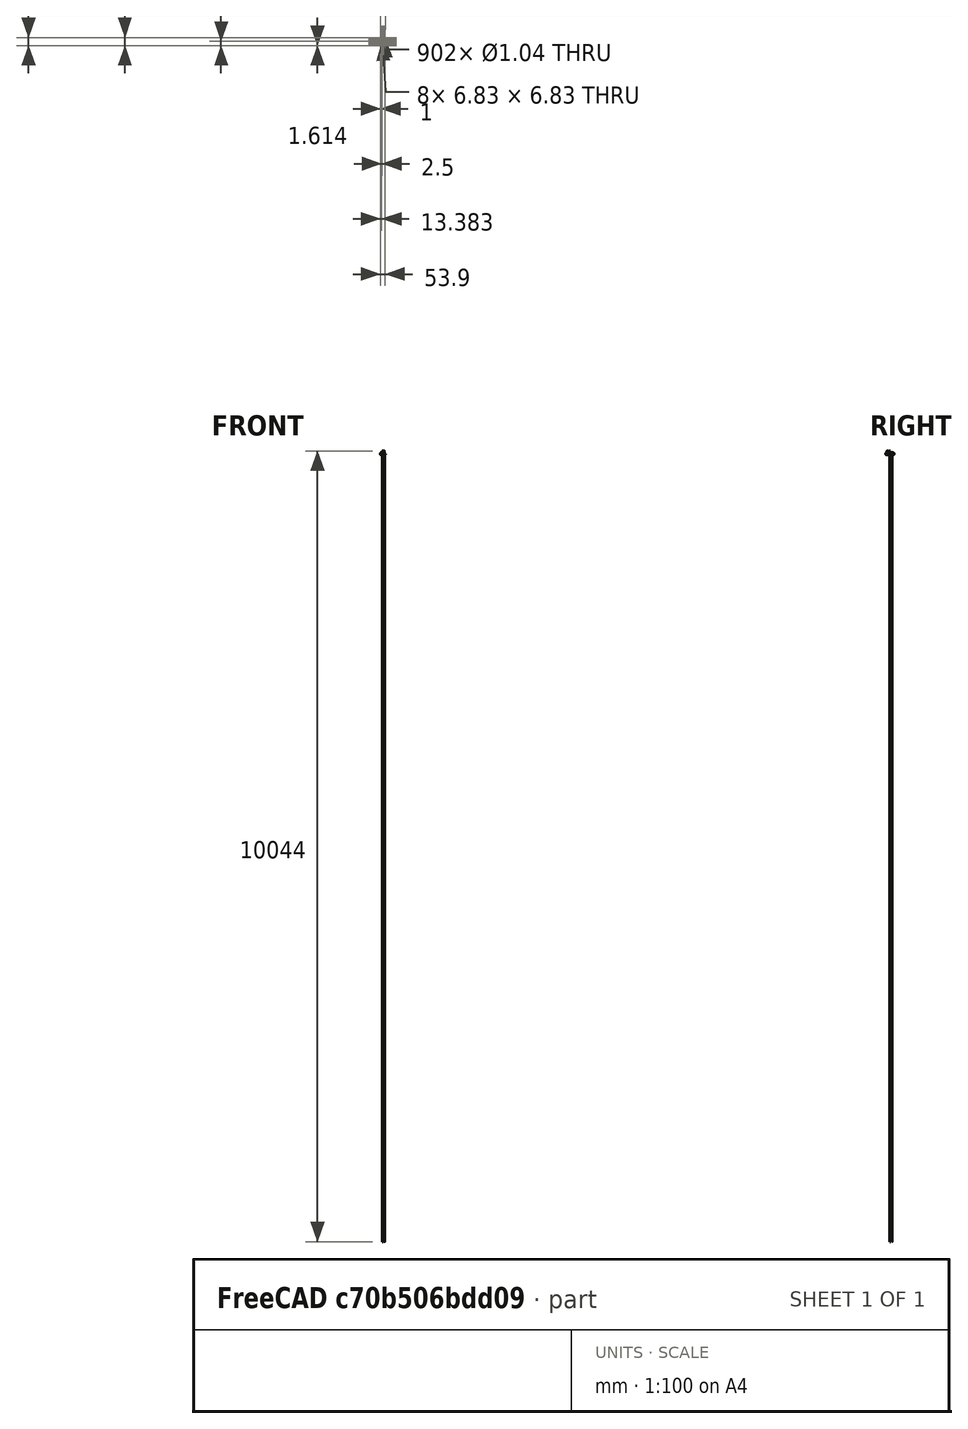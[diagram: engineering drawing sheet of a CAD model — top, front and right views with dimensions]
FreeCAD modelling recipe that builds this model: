
FCSTD DOCUMENT  (FreeCAD 0.16R6603 (Git))
Label: Layouts
License: All rights reserved
LicenseURL: http://en.wikipedia.org/wiki/All_rights_reserved
objects: PartDesign::Pad×12, Sketcher::SketchObject×10, App::DocumentObjectGroup×8, PartDesign::Pocket×5, Part::FeaturePython×4, Part::Feature×2, Part::MultiFuse×2, PartDesign::Fillet×2, PartDesign::LinearPattern×2, PartDesign::Chamfer×1, PartDesign::MultiTransform×1
note: 58 computed .brp shape members not serialized (recipe doc carries the construction recipe); baked Part::Feature solids carry a one-line shape summary decoded from their .brp

FEATURE [Part::Feature] _591A_Box
  Placement = pos=(0,0,1) rot=(1,0,0;3.14159rad)
  shape: bbox 50 x 100 x 21.01 mm, 623 faces (baked)
FEATURE [Part::Feature] _591A_Lid
  Placement = pos=(0,0,1) rot=(0,0,1;1.5708rad)
  shape: bbox 50 x 100 x 5.8 mm, 112 faces (baked)
FEATURE [App::DocumentObjectGroup] Group  label="Box"
  Group = -> [_591A_Lid,_591A_Box]
FEATURE [Sketcher::SketchObject] Sketch
  sketch-geometry (2):
    g0: Circle CenterX=0 CenterY=0 CenterZ=0 NormalX=0 NormalY=0 NormalZ=1 Radius=18.5
    g1: Circle CenterX=0 CenterY=0 CenterZ=0 NormalX=0 NormalY=0 NormalZ=1 Radius=11.5
  constraints (4):
    c: Coincident(g0,g-1)
    c: Radius(g0) = 18.5
    c: Coincident(g1,g-1)
    c: Radius(g1) = 11.5
FEATURE [PartDesign::Pad] Pad
  Length = 0.7
  Length2 = 100
  Sketch = -> Sketch
  Type = 0
FEATURE [Sketcher::SketchObject] Sketch002
  Placement = pos=(0,0,1.5) rot=(0,0,1;0rad)
  sketch-geometry (1):
    g0: Circle CenterX=2.5 CenterY=2.5 CenterZ=0 NormalX=0 NormalY=0 NormalZ=1 Radius=1.9
  constraints (1):
    c: Radius(g0) = 1.9
FEATURE [PartDesign::Pocket] Pocket
  Length = 0.3
  Sketch = -> Sketch002
  Type = 0
FEATURE [Sketcher::SketchObject] Sketch003
  ExternalGeometry = -> [Pocket]
  Placement = pos=(0,0,1.2) rot=(0,0,1;0rad)
  Support = -> Pocket [Face8]
  sketch-geometry (21):
    g0: Circle [constr] CenterX=2.5 CenterY=2.5 CenterZ=0 NormalX=0 NormalY=0 NormalZ=1 Radius=1.66517
    g1: LineSegment StartX=0.835727 StartY=2.55467 StartZ=0 EndX=1.70607 EndY=2.55467 EndZ=0
    g2: LineSegment StartX=1.70607 StartY=2.55467 StartZ=0 EndX=2.17002 EndY=3.01784 EndZ=0
    g3: LineSegment StartX=2.17002 StartY=3.01784 StartZ=0 EndX=2.17002 EndY=3.80753 EndZ=0
    g4: LineSegment StartX=2.17002 StartY=3.80753 StartZ=0 EndX=1.80001 EndY=3.80753 EndZ=0
    g5: LineSegment StartX=1.80001 StartY=3.80753 StartZ=0 EndX=1.80001 EndY=4.01089 EndZ=0
    g6: LineSegment StartX=2.43665 StartY=4.16397 StartZ=0 EndX=2.43665 EndY=2.96848 EndZ=0
    g7: LineSegment StartX=2.43665 StartY=2.96848 StartZ=0 EndX=2.93997 EndY=2.96848 EndZ=0
    g8: LineSegment StartX=2.93997 StartY=2.96848 StartZ=0 EndX=3.51249 EndY=2.38588 EndZ=0
    g9: LineSegment StartX=3.51249 StartY=2.38588 StartZ=0 EndX=4.16126 EndY=2.38588 EndZ=0
    g10: LineSegment StartX=0.847377 StartY=2.29597 StartZ=0 EndX=1.9035 EndY=2.29597 EndZ=0
    g11: LineSegment StartX=1.9035 StartY=2.29597 StartZ=0 EndX=2.26873 EndY=2.70196 EndZ=0
    g12: LineSegment StartX=2.26873 StartY=2.70196 StartZ=0 EndX=2.6537 EndY=2.70196 EndZ=0
    g13: LineSegment StartX=2.6537 StartY=2.70196 StartZ=0 EndX=3.16354 EndY=2.21375 EndZ=0
    g14: LineSegment StartX=3.16354 StartY=2.21375 StartZ=0 EndX=3.16354 EndY=0.972745 EndZ=0
    g15: ArcOfCircle CenterX=2.5 CenterY=2.5 CenterZ=0 NormalX=0 NormalY=0 NormalZ=1 Radius=1.66517 StartAngle=2.00465 EndAngle=3.10875
    g16: ArcOfCircle CenterX=2.5 CenterY=2.5 CenterZ=0 NormalX=0 NormalY=0 NormalZ=1 Radius=1.66517 StartAngle=6.2146 EndAngle=7.89204
    g17: LineSegment StartX=3.41498 StartY=1.10874 StartZ=0 EndX=3.41498 EndY=2.17405 EndZ=0
    g18: LineSegment StartX=3.41498 StartY=2.17405 StartZ=0 EndX=4.13296 EndY=2.17405 EndZ=0
    g19: ArcOfCircle CenterX=2.5 CenterY=2.5 CenterZ=0 NormalX=0 NormalY=0 NormalZ=1 Radius=1.66517 StartAngle=5.29413 EndAngle=6.08617
    g20: ArcOfCircle CenterX=2.5 CenterY=2.5 CenterZ=0 NormalX=0 NormalY=0 NormalZ=1 Radius=1.66517 StartAngle=3.26443 EndAngle=5.12225
  constraints (43):
    c: Coincident(g0,g-3)
    c: PointOnObject(g1,g0)
    c: Horizontal(g1)
    c: Coincident(g1,g2)
    c: Coincident(g2,g3)
    c: Vertical(g3)
    c: Coincident(g3,g4)
    c: Horizontal(g4)
    c: Coincident(g4,g5)
    c: PointOnObject(g5,g0)
    c: PointOnObject(g6,g0)
    c: Vertical(g6)
    c: Coincident(g6,g7)
    c: Horizontal(g7)
    c: Coincident(g7,g8)
    c: Coincident(g8,g9)
    c: PointOnObject(g9,g0)
    c: Horizontal(g9)
    c: PointOnObject(g10,g0)
    c: Horizontal(g10)
    c: Coincident(g10,g11)
    c: Coincident(g11,g12)
    c: Horizontal(g12)
    c: Coincident(g12,g13)
    c: Coincident(g13,g14)
    c: PointOnObject(g14,g0)
    c: Vertical(g14)
    c: Vertical(g5)
    c: Coincident(g15,g1)
    c: Coincident(g15,g5)
    c: Coincident(g16,g6)
    c: Coincident(g16,g9)
    c: PointOnObject(g17,g0)
    c: Vertical(g17)
    c: Coincident(g17,g18)
    c: PointOnObject(g18,g0)
    c: Horizontal(g18)
    c: Coincident(g19,g18)
    c: Coincident(g19,g17)
    c: Tangent(g19,g0)
    c: Coincident(g20,g10)
    c: Coincident(g20,g14)
    c: Tangent(g20,g0)
FEATURE [PartDesign::Pad] Pad002
  Length = 0.1
  Length2 = 100
  Sketch = -> Sketch003
  Type = 0
FEATURE [Part::FeaturePython] Array  # Draft array (typed FeaturePython)
  Angle = 360
  ArrayType = 1
  Axis = (0,0,1)
  Base = -> Pad002
  Center = (-12,0,0)
  Fuse = false
  IntervalAxis = (0,0,0)
  IntervalX = (1,0,0)
  IntervalY = (0,1,0)
  IntervalZ = (0,0,1)
  NumberPolar = 12
  NumberX = 0
  NumberY = 0
  NumberZ = 0
  Placement = pos=(12,0,0) rot=(0,0,1;0rad)
FEATURE [Part::MultiFuse] Fusion
  Placement = pos=(0,-3,22) rot=(0,0,1;0rad)
  Shapes = -> [Array,Pad]
FEATURE [App::DocumentObjectGroup] Group001  label="Neopixel"
  Group = -> [Pocket,Fusion]
FEATURE [PartDesign::Pad] Pad003
  Length = 1
  Length2 = 100
  Placement = pos=(-6,-10,14) rot=(0,0,1;0rad)
  Type = 0
FEATURE [App::DocumentObjectGroup] Group002  label="Knob"
  Group = -> [Pad003]
FEATURE [PartDesign::Pocket] Pocket001
  Length = 1
  Placement = pos=(8,-36,16.3) rot=(0,0,1;0rad)
  Type = 0
FEATURE [PartDesign::Pocket] Pocket002
  Length = 1
  Placement = pos=(-19,-36,36) rot=(0,0,1;0rad)
  Type = 0
FEATURE [PartDesign::Pad] Pad004
  Length = 1
  Length2 = 100
  Placement = pos=(-6,-29,14) rot=(0,0,1;0rad)
  Type = 0
FEATURE [App::DocumentObjectGroup] Group005
FEATURE [Sketcher::SketchObject] Sketch004
  sketch-geometry (4):
    g0: LineSegment StartX=0 StartY=0 StartZ=0 EndX=27 EndY=0 EndZ=0
    g1: LineSegment StartX=27 StartY=0 StartZ=0 EndX=27 EndY=27.3 EndZ=0
    g2: LineSegment StartX=27 StartY=27.3 StartZ=0 EndX=0 EndY=27.3 EndZ=0
    g3: LineSegment StartX=0 StartY=27.3 StartZ=0 EndX=0 EndY=0 EndZ=0
  constraints (11):
    c: Coincident(g0,g1)
    c: Coincident(g1,g2)
    c: Coincident(g2,g3)
    c: Coincident(g3,g0)
    c: Horizontal(g0)
    c: Horizontal(g2)
    c: Vertical(g1)
    c: Vertical(g3)
    c: Coincident(g0,g-1)
    c: DistanceX(g2) = -27
    c: DistanceY(g1) = 27.3
FEATURE [PartDesign::Pad] Pad005
  Length = 1
  Length2 = 100
  Sketch = -> Sketch004
  Type = 0
FEATURE [Sketcher::SketchObject] Sketch001
  ExternalGeometry = -> [Pad005]
  Placement = pos=(0,0,1) rot=(0,0,1;0rad)
  Support = -> Pad005 [Face6]
  sketch-geometry (16):
    g0: ArcOfCircle CenterX=1.75 CenterY=25.175 CenterZ=0 NormalX=0 NormalY=0 NormalZ=1 Radius=1.125 StartAngle=1.5708 EndAngle=4.71239
    g1: ArcOfCircle CenterX=3 CenterY=25.175 CenterZ=0 NormalX=0 NormalY=0 NormalZ=1 Radius=1.125 StartAngle=4.71239 EndAngle=7.85398
    g2: LineSegment StartX=1.75 StartY=24.05 StartZ=0 EndX=3 EndY=24.05 EndZ=0
    g3: LineSegment StartX=1.75 StartY=26.3 StartZ=0 EndX=3 EndY=26.3 EndZ=0
    g4: ArcOfCircle CenterX=24 CenterY=25.175 CenterZ=0 NormalX=0 NormalY=0 NormalZ=1 Radius=1.125 StartAngle=1.5708 EndAngle=4.71239
    g5: ArcOfCircle CenterX=25.25 CenterY=25.175 CenterZ=0 NormalX=0 NormalY=0 NormalZ=1 Radius=1.125 StartAngle=4.71239 EndAngle=7.85398
    g6: LineSegment StartX=24 StartY=24.05 StartZ=0 EndX=25.25 EndY=24.05 EndZ=0
    g7: LineSegment StartX=24 StartY=26.3 StartZ=0 EndX=25.25 EndY=26.3 EndZ=0
    g8: ArcOfCircle CenterX=1.75 CenterY=2.125 CenterZ=0 NormalX=0 NormalY=0 NormalZ=1 Radius=1.125 StartAngle=1.5708 EndAngle=4.71239
    g9: ArcOfCircle CenterX=3 CenterY=2.125 CenterZ=0 NormalX=0 NormalY=0 NormalZ=1 Radius=1.125 StartAngle=4.71239 EndAngle=7.85398
    g10: LineSegment StartX=1.75 StartY=1 StartZ=0 EndX=3 EndY=1 EndZ=0
    g11: LineSegment StartX=1.75 StartY=3.25 StartZ=0 EndX=3 EndY=3.25 EndZ=0
    g12: ArcOfCircle CenterX=24 CenterY=2.125 CenterZ=0 NormalX=0 NormalY=0 NormalZ=1 Radius=1.125 StartAngle=1.5708 EndAngle=4.71239
    g13: ArcOfCircle CenterX=25.25 CenterY=2.125 CenterZ=0 NormalX=0 NormalY=0 NormalZ=1 Radius=1.125 StartAngle=4.71239 EndAngle=7.85398
    g14: LineSegment StartX=24 StartY=1 StartZ=0 EndX=25.25 EndY=1 EndZ=0
    g15: LineSegment StartX=24 StartY=3.25 StartZ=0 EndX=25.25 EndY=3.25 EndZ=0
  constraints (40):
    c: Tangent(g0,g3) = 1.5708
    c: Tangent(g0,g2) = -1.5708
    c: Tangent(g2,g1) = -1.5708
    c: Tangent(g3,g1) = 1.5708
    c: Horizontal(g2)
    c: Equal(g0,g1)
    c: DistanceY(g0,g0) = -2.25
    c: DistanceX(g0,g1) = 1.25
    c: DistanceY(g-3,g0) = -1
    c: DistanceX(g0,g-3) = -1.75
    c: Tangent(g4,g7) = 1.5708
    c: Tangent(g4,g6) = -1.5708
    c: Tangent(g6,g5) = -1.5708
    c: Tangent(g7,g5) = 1.5708
    c: Horizontal(g6)
    c: Equal(g4,g5)
    c: Equal(g6,g2)
    c: Equal(g4,g0)
    c: DistanceX(g-3,g5) = -1.75
    c: DistanceY(g5,g-3) = 1
    c: Tangent(g8,g11) = 1.5708
    c: Tangent(g8,g10) = -1.5708
    c: Tangent(g10,g9) = -1.5708
    c: Tangent(g11,g9) = 1.5708
    c: Horizontal(g10)
    c: Equal(g8,g9)
    c: Equal(g2,g11)
    c: Equal(g9,g0)
    c: DistanceX(g-1,g8) = 1.75
    c: DistanceY(g-1,g8) = 1
    c: Tangent(g12,g15) = 1.5708
    c: Tangent(g12,g14) = -1.5708
    c: Tangent(g14,g13) = -1.5708
    c: Tangent(g15,g13) = 1.5708
    c: Horizontal(g14)
    c: Equal(g12,g13)
    c: Equal(g15,g10)
    c: Equal(g12,g9)
    c: DistanceX(g13,g-4) = 1.75
    c: DistanceY(g13,g-4) = -1
FEATURE [PartDesign::Pocket] Pocket003
  Length = 5
  Sketch = -> Sketch001
  Type = 1
FEATURE [Sketcher::SketchObject] Sketch005
  ExternalGeometry = -> [Pocket003]
  Placement = pos=(0,0,1) rot=(0,0,1;0rad)
  Support = -> Pocket003 [Face5]
  sketch-geometry (4):
    g0: LineSegment StartX=0 StartY=23.1 StartZ=0 EndX=27 EndY=23.1 EndZ=0
    g1: LineSegment StartX=27 StartY=23.1 StartZ=0 EndX=27 EndY=4.1 EndZ=0
    g2: LineSegment StartX=27 StartY=4.1 StartZ=0 EndX=0 EndY=4.1 EndZ=0
    g3: LineSegment StartX=0 StartY=4.1 StartZ=0 EndX=0 EndY=23.1 EndZ=0
  constraints (12):
    c: Coincident(g0,g1)
    c: Coincident(g1,g2)
    c: Coincident(g2,g3)
    c: Coincident(g3,g0)
    c: Horizontal(g0)
    c: Horizontal(g2)
    c: Vertical(g1)
    c: Vertical(g3)
    c: PointOnObject(g0,g-2)
    c: PointOnObject(g1,g-4)
    c: DistanceY(g0,g-4) = 4.2
    c: DistanceY(g3) = 19
FEATURE [PartDesign::Pad] Pad001
  Length = 1.6
  Length2 = 100
  Sketch = -> Sketch005
  Type = 0
FEATURE [Sketcher::SketchObject] Sketch006
  ExternalGeometry = -> [Pad001]
  Placement = pos=(0,0,1) rot=(0,0,1;0rad)
  Support = -> Pad001 [Face7]
  sketch-geometry (4):
    g0: Circle CenterX=9.5 CenterY=25.55 CenterZ=0 NormalX=0 NormalY=0 NormalZ=1 Radius=0.9
    g1: Circle CenterX=11.95 CenterY=25.55 CenterZ=0 NormalX=0 NormalY=0 NormalZ=1 Radius=0.9
    g2: Circle CenterX=14.4 CenterY=25.55 CenterZ=0 NormalX=0 NormalY=0 NormalZ=1 Radius=0.9
    g3: Circle CenterX=16.85 CenterY=25.55 CenterZ=0 NormalX=0 NormalY=0 NormalZ=1 Radius=0.9
  constraints (12):
    c: DistanceX(g-4,g0) = 9.5
    c: DistanceX(g0,g1) = 2.45
    c: DistanceX(g1,g2) = 2.45
    c: DistanceX(g2,g3) = 2.45
    c: Radius(g0) = 0.9
    c: Equal(g0,g1)
    c: Equal(g1,g2)
    c: Equal(g2,g3)
    c: DistanceY(g-4,g0) = -1.75
    c: DistanceY(g1,g-5) = 1.75
    c: DistanceY(g2,g-5) = 1.75
    c: DistanceY(g3,g-5) = 1.75
FEATURE [PartDesign::Pad] Pad006
  Length = 0.5
  Length2 = 100
  Sketch = -> Sketch006
  Type = 0
FEATURE [Part::FeaturePython] Clone  label="Clone of LinearPattern"  # WARN: FeaturePython — macro-defined, semantics opaque (R4)
  Placement = pos=(-13,17,20) rot=(0,0,1;0rad)
  Scale = (1,1,1)
FEATURE [PartDesign::Fillet] Fillet
  Base = -> Pad001 [Edge1]
  Placement = pos=(29.3,0,0) rot=(0.57735,0.57735,0.57735;2.0944rad)
  Radius = 0.3
FEATURE [PartDesign::Fillet] Fillet001
  Base = -> Fillet [Edge3]
  Placement = pos=(29.3,0,0) rot=(0.57735,0.57735,0.57735;2.0944rad)
  Radius = 0.3
FEATURE [PartDesign::Pad] Pad007
  Length = 0.7
  Length2 = 100
  Sketch = -> Sketch003
  Type = 0
FEATURE [Part::MultiFuse] Fusion001
  Shapes = -> [Pad007,Fillet001]
FEATURE [App::DocumentObjectGroup] Group006
  Group = -> [Fillet,Fusion001]
FEATURE [PartDesign::Pad] Pad008
  Length = 2.5
  Length2 = 100
  Sketch = -> Sketch002
  Type = 0
FEATURE [PartDesign::Pad] Pad009  label="button_pad002"
  Length = 2.5
  Length2 = 100
  Sketch = -> Sketch002
  Type = 0
FEATURE [Part::FeaturePython] Clone001  label="Clone of button_pad002"  # Draft clone (typed FeaturePython)
  Objects = -> [Pad009]
  Placement = pos=(14,-30,39) rot=(0,0,1;0rad)
  Scale = (1,1,1)
FEATURE [App::DocumentObjectGroup] Group004  label="buttons"
  Group = -> [Pocket001,Pocket002,Pad009,Clone001]
FEATURE [Sketcher::SketchObject] Sketch007
  sketch-geometry (1):
    g0: Circle CenterX=0 CenterY=0 CenterZ=0 NormalX=0 NormalY=0 NormalZ=1 Radius=7.25
  constraints (2):
    c: Coincident(g0,g-1)
    c: Radius(g0) = 7.25
FEATURE [PartDesign::Pad] Pad010
  Length = 16.91
  Length2 = 100
  Sketch = -> Sketch007
  Type = 0
FEATURE [PartDesign::Chamfer] Chamfer
  Base = -> Pad010 [Edge3]
  Size = 1
FEATURE [Part::FeaturePython] Clone002  label="Clone of Chamfer"  # Draft clone (typed FeaturePython)
  Objects = -> [Chamfer]
  Placement = pos=(0,-3,25) rot=(0,0,1;0rad)
  Scale = (1,1,1)
FEATURE [App::DocumentObjectGroup] Group007
  Group = -> [Pad010,Chamfer,Clone002]
FEATURE [Sketcher::SketchObject] Sketch008
  sketch-geometry (4):
    g0: LineSegment StartX=-27.19 StartY=51.7638 StartZ=0 EndX=28.81 EndY=51.7638 EndZ=0
    g1: LineSegment StartX=28.81 StartY=51.7638 StartZ=0 EndX=28.81 EndY=-51.2362 EndZ=0
    g2: LineSegment StartX=28.81 StartY=-51.2362 StartZ=0 EndX=-27.19 EndY=-51.2362 EndZ=0
    g3: LineSegment StartX=-27.19 StartY=-51.2362 StartZ=0 EndX=-27.19 EndY=51.7638 EndZ=0
  constraints (10):
    c: Coincident(g0,g1)
    c: Coincident(g1,g2)
    c: Coincident(g2,g3)
    c: Coincident(g3,g0)
    c: Horizontal(g0)
    c: Horizontal(g2)
    c: Vertical(g1)
    c: Vertical(g3)
    c: DistanceX(g0) = 56
    c: DistanceY(g3) = 103
FEATURE [PartDesign::Pad] Pad011
  Length = 0.1
  Length2 = 100
  Sketch = -> Sketch008
  Type = 0
FEATURE [Sketcher::SketchObject] Sketch009
  ExternalGeometry = -> [Pad011]
  Placement = pos=(0,0,0.1) rot=(0,0,1;0rad)
  Support = -> Pad011 [Face6]
  sketch-geometry (1):
    g0: Circle CenterX=-26.19 CenterY=50.7638 CenterZ=0 NormalX=0 NormalY=0 NormalZ=1 Radius=0.522082
  constraints (2):
    c: DistanceX(g-3,g0) = 1
    c: DistanceY(g0,g-3) = 1
FEATURE [PartDesign::Pocket] Pocket004
  Length = 5
  Sketch = -> Sketch009
  Type = 1
FEATURE [App::DocumentObjectGroup] Group008
  Group = -> [Pad011,Pocket004]
FEATURE [PartDesign::LinearPattern] LinearPattern
  Direction = -> Sketch009 [H_Axis]
  Length = 53.9
  Occurrences = 22
FEATURE [PartDesign::LinearPattern] LinearPattern001
  Direction = -> Sketch009 [V_Axis]
  Length = 102.9
  Occurrences = 42
  Reversed = true
FEATURE [PartDesign::MultiTransform] MultiTransform
  Originals = -> [Pocket004]
  Transformations = -> [LinearPattern,LinearPattern001]
